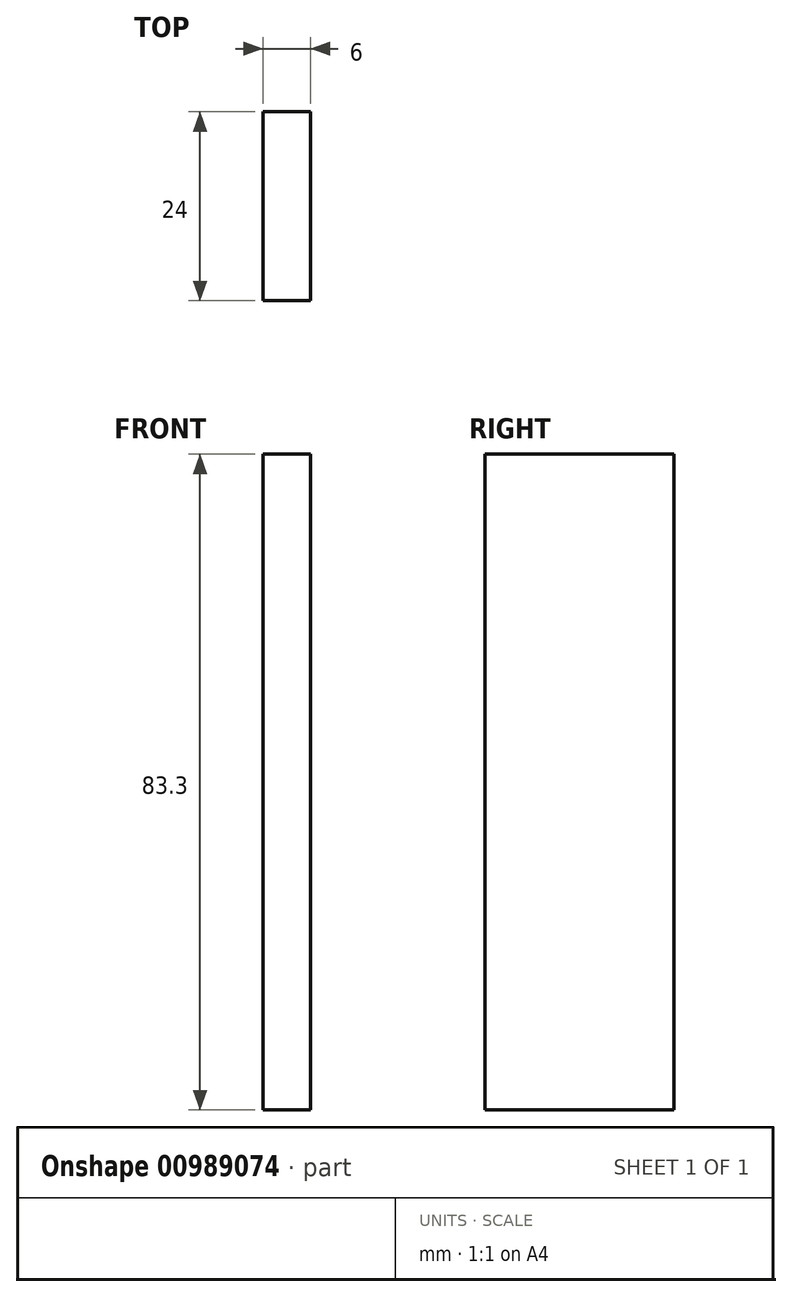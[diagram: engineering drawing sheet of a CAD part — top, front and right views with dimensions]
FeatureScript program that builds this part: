
annotation { "Feature Type Name" : "Feature", "Feature Type Description" : "" }
export const myFeature = defineFeature(function(context is Context, id is Id, definition is map)
    precondition{}
    {
        {
            var Q0;
            Q0=qCreatedBy(makeId("Front.planeOp"),FACE);
            var sketch = newSketch(context, id + "F0", { "sketchPlane" : qUnion([Q0])});
            skLineSegment(sketch, "E0.bottom", {"start": v(0, 0) * mm, "end": v(-6, 0) * mm});
            skLineSegment(sketch, "E0.top", {"start": v(0, 83.3) * mm, "end": v(-6, 83.3) * mm});
            skLineSegment(sketch, "E0.left", {"start": v(0, 0) * mm, "end": v(0, 83.3) * mm});
            skLineSegment(sketch, "E0.right", {"start": v(-6, 0) * mm, "end": v(-6, 83.3) * mm});
            skSolve(sketch);
        }
        {
            var Q0;
            Q0=makeQuery(id+"F0.imprint","IMPRINT",FACE,{"disambiguationData":[TD([[makeQuery(id+"F0.imprint","IMPRINT",EDGE,{"derivedFrom":sQuery(id+"F0.wireOp",EDGE,"E0.bottom")}),-1.0]])]});
            extrude(context, id + "F1", {"entities" : qUnion([Q0]), "depth" : (30 - 6) * mm, "offsetDistance" : 25 * mm});
        }
    });
